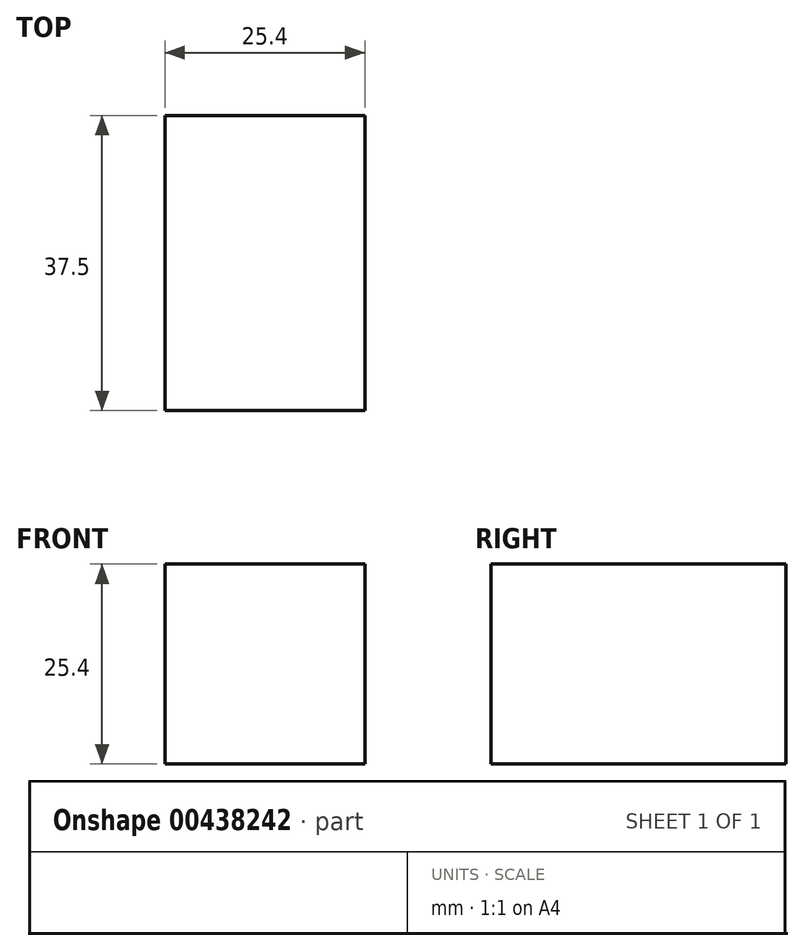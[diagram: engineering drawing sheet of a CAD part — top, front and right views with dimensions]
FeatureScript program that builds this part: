
annotation { "Feature Type Name" : "Feature", "Feature Type Description" : "" }
export const myFeature = defineFeature(function(context is Context, id is Id, definition is map)
    precondition{}
    {
        {
            var Q0;
            Q0=qCreatedBy(makeId("Top.planeOp"),FACE);
            var sketch = newSketch(context, id + "F0", { "sketchPlane" : qUnion([Q0])});
            skLineSegment(sketch, "E0.bottom", {"start": v(-59.91, 42.52) * mm, "end": v(-34.51, 42.52) * mm});
            skLineSegment(sketch, "E0.top", {"start": v(-59.91, 5.02) * mm, "end": v(-34.51, 5.02) * mm});
            skLineSegment(sketch, "E0.left", {"start": v(-59.91, 42.52) * mm, "end": v(-59.91, 5.02) * mm});
            skLineSegment(sketch, "E0.right", {"start": v(-34.51, 42.52) * mm, "end": v(-34.51, 5.02) * mm});
            skSolve(sketch);
        }
        {
            var Q0;
            Q0=makeQuery(id+"F0.imprint","IMPRINT",FACE,{"disambiguationData":[TD([[makeQuery(id+"F0.imprint","IMPRINT",EDGE,{"derivedFrom":sQuery(id+"F0.wireOp",EDGE,"E0.bottom")}),-1.0]])]});
            extrude(context, id + "F1", {"entities" : qUnion([Q0]), "depth" : 25.4 * mm});
        }
    });
